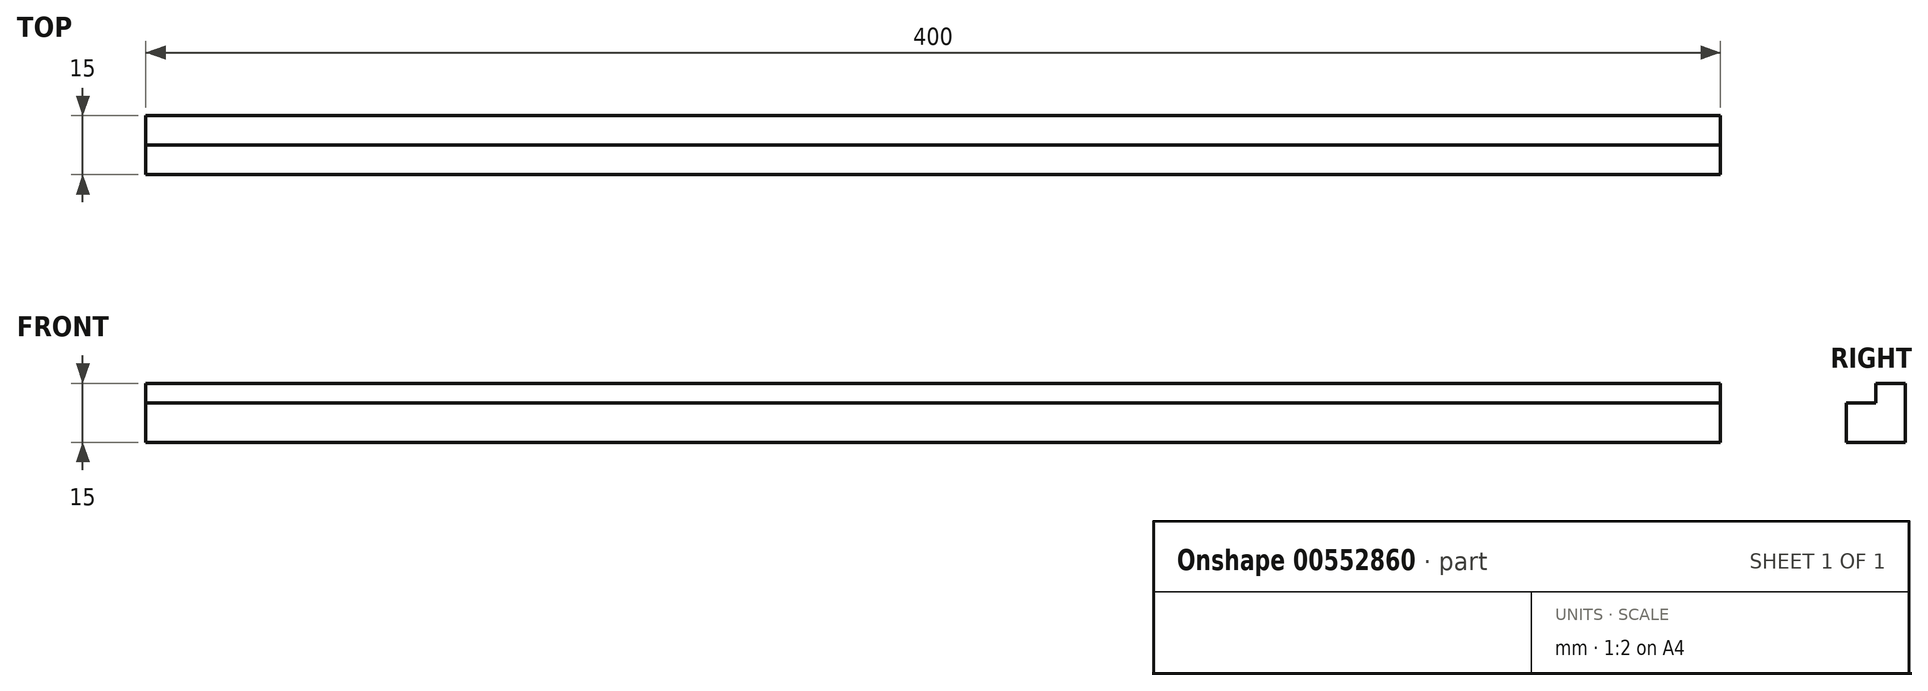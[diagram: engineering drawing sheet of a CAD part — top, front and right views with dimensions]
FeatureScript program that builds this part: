
annotation { "Feature Type Name" : "Feature", "Feature Type Description" : "" }
export const myFeature = defineFeature(function(context is Context, id is Id, definition is map)
    precondition{}
    {
        {
            var Q0;
            Q0=qCreatedBy(makeId("Top.planeOp"),FACE);
            var sketch = newSketch(context, id + "F0", { "sketchPlane" : qUnion([Q0])});
            skLineSegment(sketch, "E0.bottom", {"start": v(-131.03, 24.6) * mm, "end": v(268.97, 24.6) * mm});
            skLineSegment(sketch, "E0.top", {"start": v(-131.03, 9.6) * mm, "end": v(268.97, 9.6) * mm});
            skLineSegment(sketch, "E0.left", {"start": v(-131.03, 24.6) * mm, "end": v(-131.03, 9.6) * mm});
            skLineSegment(sketch, "E0.right", {"start": v(268.97, 24.6) * mm, "end": v(268.97, 9.6) * mm});
            skSolve(sketch);
        }
        {
            var Q0;
            Q0=makeQuery(id+"F0.imprint","IMPRINT",FACE,{"disambiguationData":[TD([[makeQuery(id+"F0.imprint","IMPRINT",EDGE,{"derivedFrom":sQuery(id+"F0.wireOp",EDGE,"E0.bottom")}),-1.0]])]});
            extrude(context, id + "F1", {"entities" : qUnion([Q0]), "depth" : 15 * mm, "offsetDistance" : 25 * mm});
        }
        {
            var Q0;
            Q0=makeQuery(id+"F1.opExtrude","SWEPT_FACE",FACE,{"disambiguationData":[OSD([sQuery(id+"F0.wireOp",EDGE,"E0.right")])]});
            var sketch = newSketch(context, id + "F2", { "sketchPlane" : qUnion([Q0])});
            skPoint(sketch, "E1.oppositeSnap0", {"position": v(17.1, 15) * mm});
            skLineSegment(sketch, "E1.bottom", {"start": v(9.6, 15) * mm, "end": v(17.1, 15) * mm});
            skLineSegment(sketch, "E1.top", {"start": v(9.6, 10) * mm, "end": v(17.1, 10) * mm});
            skLineSegment(sketch, "E1.left", {"start": v(9.6, 15) * mm, "end": v(9.6, 10) * mm});
            skLineSegment(sketch, "E1.right", {"start": v(17.1, 15) * mm, "end": v(17.1, 10) * mm});
            skSolve(sketch);
        }
        {
            var Q0;
            Q0=makeQuery(id+"F2.imprint","IMPRINT",FACE,{"disambiguationData":[TD([[makeQuery(id+"F2.imprint","IMPRINT",EDGE,{"derivedFrom":sQuery(id+"F2.wireOp",EDGE,"E1.bottom")}),1.0]])]});
            extrude(context, id + "F3", {"entities" : qUnion([Q0]), "operationType" : NewBodyOperationType.REMOVE, "endBound" : BoundingType.UP_TO_NEXT, "oppositeDirection" : true, "depth" : 25 * mm, "offsetDistance" : 25 * mm});
        }
    });
